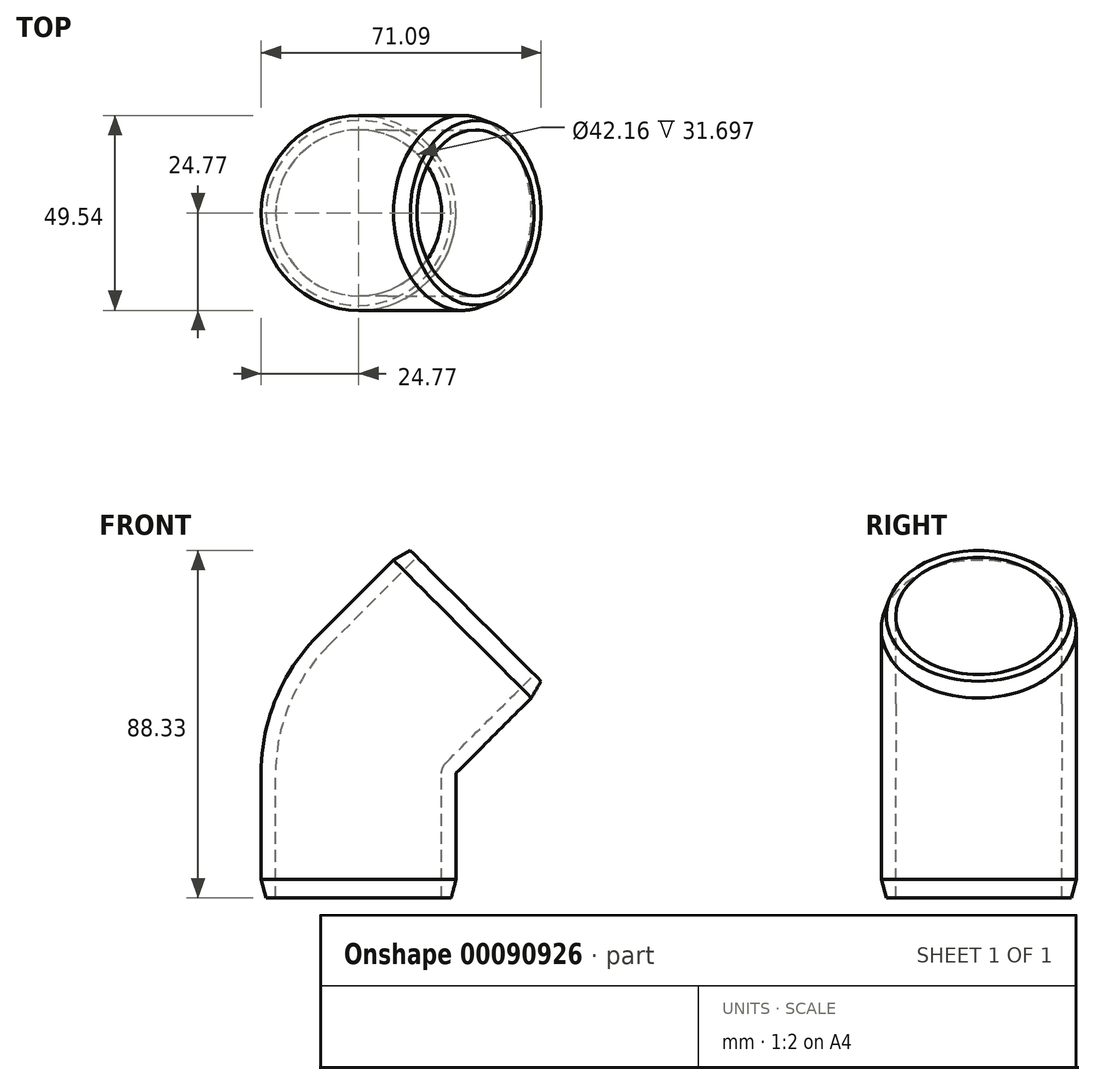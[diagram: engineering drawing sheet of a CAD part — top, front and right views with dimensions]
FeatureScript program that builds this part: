
annotation { "Feature Type Name" : "Feature", "Feature Type Description" : "" }
export const myFeature = defineFeature(function(context is Context, id is Id, definition is map)
    precondition{}
    {
        {
            var Q0;
            Q0=qCreatedBy(makeId("Front.planeOp"),FACE);
            var sketch = newSketch(context, id + "F0", { "sketchPlane" : qUnion([Q0])});
            skLineSegment(sketch, "E0", {"start": v(24.77, -42) * mm, "end": v(24.77, -10.26) * mm});
            skLineSegment(sketch, "E1", {"start": v(24.77, -10.26) * mm, "end": v(47.22, 12.2) * mm});
            skLineSegment(sketch, "E2.0", {"start": v(7.3, 7.3) * mm, "end": v(29.7, 29.7) * mm});
            skLineSegment(sketch, "E2.1", {"start": v(0, -42) * mm, "end": v(0, -10.31) * mm});
            skLineSegment(sketch, "E3", {"start": v(47.22, 12.2) * mm, "end": v(22.21, 37.2) * mm, "construction": true});
            skLineSegment(sketch, "E4", {"start": v(24.77, -42) * mm, "end": v(-17.96, -42) * mm, "construction": true});
            skPoint(sketch, "E5.visualSharp", {"position": v(0, 0) * mm});
            skArc(sketch, "E5.filletArc", {"start": v(7.3, 7.3) * mm, "mid": v(1.9, -0.78) * mm, "end": v(0, -10.31) * mm});
            skSolve(sketch);
        }
        {
            var Q0;
            Q0=sQuery(id+"F0.wireOp",VERTEX,"E2.1.start");
            var Q1;
            Q1=qCreatedBy(makeId("Top.planeOp"),FACE);
            cPlane(context, id + "F1", {"entities" : qUnion([Q0, Q1]), "cplaneType" : CPlaneType.PLANE_POINT, "offset" : 152.4 * mm, "width" : 152.4 * mm, "height" : 152.4 * mm});
        }
        {
            var Q0;
            Q0=qCreatedBy(id+"F1.planeOp",FACE);
            var sketch = newSketch(context, id + "F2", { "sketchPlane" : qUnion([Q0])});
            skCircle(sketch, "E6", {"center": v(0, 0) * mm, "radius": 21.08 * mm});
            skCircle(sketch, "E7", {"center": v(0, 0) * mm, "radius": 24.77 * mm});
            skSolve(sketch);
        }
        {
            var Q0;
            Q0=makeQuery(id+"F2.imprint","IMPRINT",FACE,{"disambiguationData":[TD([[makeQuery(id+"F2.imprint","IMPRINT",EDGE,{"derivedFrom":sQuery(id+"F2.wireOp",EDGE,"E6")}),-1.0]])]});
            var Q1;
            Q1=sQuery(id+"F0.wireOp",EDGE,"E2.1");
            var Q2;
            Q2=sQuery(id+"F0.wireOp",EDGE,"E5.filletArc");
            var Q3;
            Q3=sQuery(id+"F0.wireOp",EDGE,"E2.0");
            sweep(context, id + "F3", {"profiles" : qUnion([Q0]), "path" : qUnion([Q1, Q2, Q3])});
        }
        {
            var Q0;
            Q0=makeQuery(id+"F3.opSweep","CAP_EDGE",EDGE,{"disambiguationData":[OSD([sQuery(id+"F0.wireOp",VERTEX,"E2.0.end"),sQuery(id+"F2.wireOp",EDGE,"E7")])],"isStart":false});
            chamfer(context, id + "F4", {"entities" : qUnion([Q0]), "chamferType" : ChamferType.OFFSET_ANGLE, "width" : 1.27 * mm, "oppositeDirection" : false, "angle" : 75 * degree, "tangentPropagation" : true});
        }
        {
            var Q0;
            Q0=makeQuery(id+"F3.opSweep","CAP_EDGE",EDGE,{"disambiguationData":[OSD([sQuery(id+"F0.wireOp",VERTEX,"E2.1.start"),sQuery(id+"F2.wireOp",EDGE,"E7")])],"isStart":true});
            chamfer(context, id + "F5", {"entities" : qUnion([Q0]), "chamferType" : ChamferType.OFFSET_ANGLE, "width" : 1.27 * mm, "oppositeDirection" : true, "angle" : 75 * degree, "tangentPropagation" : true});
        }
    });
